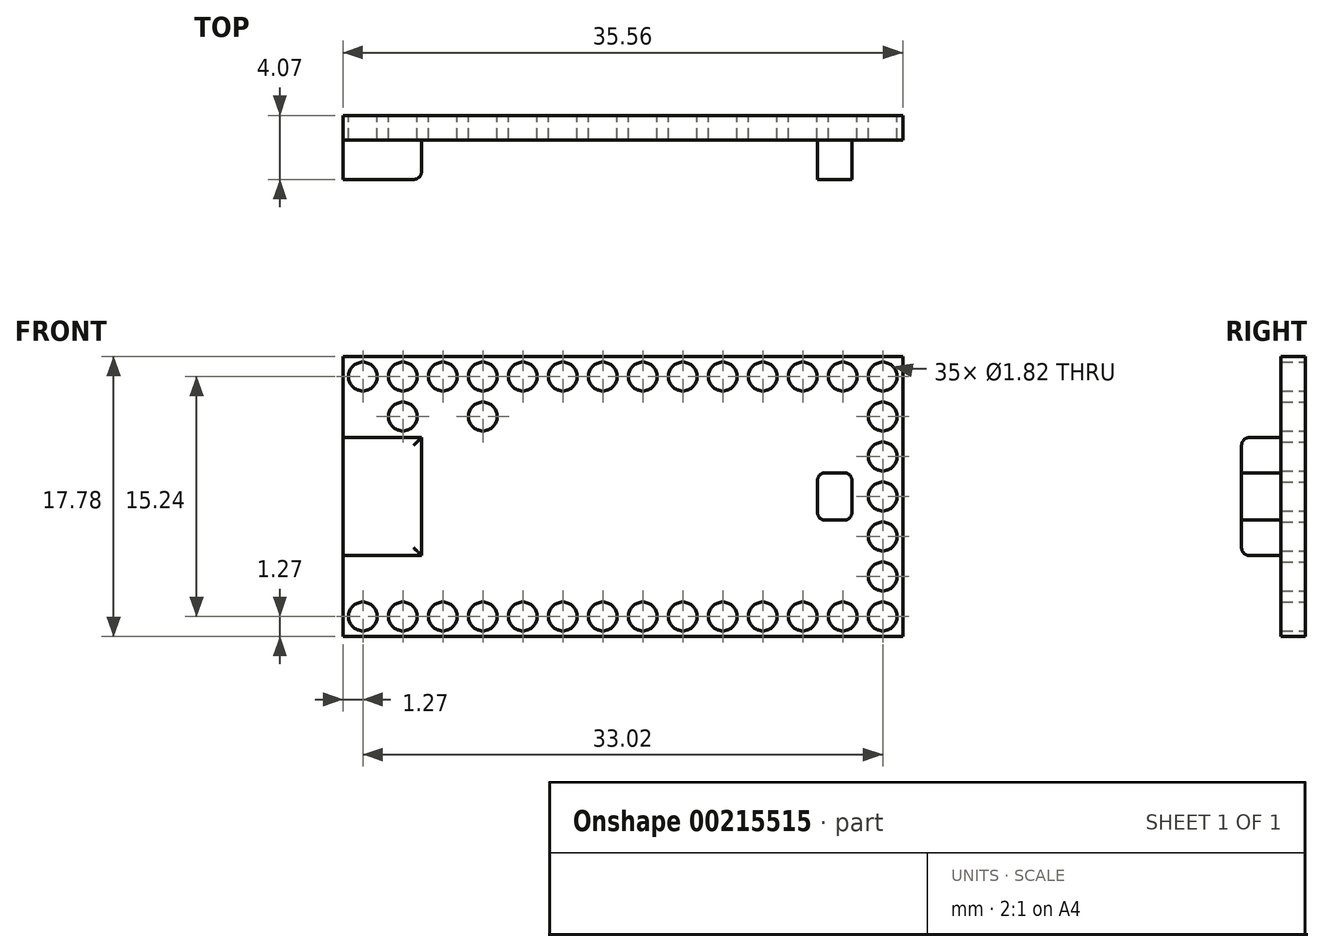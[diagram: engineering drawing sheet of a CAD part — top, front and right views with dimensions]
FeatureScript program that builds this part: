
annotation { "Feature Type Name" : "Feature", "Feature Type Description" : "" }
export const myFeature = defineFeature(function(context is Context, id is Id, definition is map)
    precondition{}
    {
        {
            var Q0;
            Q0=qCreatedBy(makeId("Front.planeOp"),FACE);
            var sketch = newSketch(context, id + "F0", { "sketchPlane" : qUnion([Q0])});
            skLineSegment(sketch, "E0.bottom", {"start": v(0, 0) * mm, "end": v(35.56, 0) * mm});
            skLineSegment(sketch, "E0.top", {"start": v(0, 17.78) * mm, "end": v(35.56, 17.78) * mm});
            skLineSegment(sketch, "E0.left", {"start": v(0, 0) * mm, "end": v(0, 17.78) * mm});
            skLineSegment(sketch, "E0.right", {"start": v(35.56, 0) * mm, "end": v(35.56, 17.78) * mm});
            skCircle(sketch, "E1", {"center": v(1.27, 16.51) * mm, "radius": 0.91 * mm});
            skCircle(sketch, "E2", {"center": v(3.8, 16.51) * mm, "radius": 0.91 * mm});
            skCircle(sketch, "E3.1.0.0", {"center": v(6.35, 16.51) * mm, "radius": 0.91 * mm});
            skCircle(sketch, "E3.2.0.0", {"center": v(8.89, 16.51) * mm, "radius": 0.91 * mm});
            skCircle(sketch, "E3.3.0.0", {"center": v(11.43, 16.51) * mm, "radius": 0.91 * mm});
            skCircle(sketch, "E3.4.0.0", {"center": v(13.97, 16.51) * mm, "radius": 0.91 * mm});
            skCircle(sketch, "E3.5.0.0", {"center": v(16.51, 16.51) * mm, "radius": 0.91 * mm});
            skCircle(sketch, "E3.6.0.0", {"center": v(19.05, 16.51) * mm, "radius": 0.91 * mm});
            skCircle(sketch, "E3.7.0.0", {"center": v(21.59, 16.51) * mm, "radius": 0.91 * mm});
            skCircle(sketch, "E3.8.0.0", {"center": v(24.13, 16.51) * mm, "radius": 0.91 * mm});
            skCircle(sketch, "E3.9.0.0", {"center": v(26.67, 16.51) * mm, "radius": 0.91 * mm});
            skCircle(sketch, "E3.10.0.0", {"center": v(29.21, 16.51) * mm, "radius": 0.91 * mm});
            skCircle(sketch, "E3.11.0.0", {"center": v(31.75, 16.51) * mm, "radius": 0.91 * mm});
            skCircle(sketch, "E3.12.0.0", {"center": v(34.3, 16.51) * mm, "radius": 0.91 * mm});
            skLineSegment(sketch, "E3.direction1", {"start": v(3.8, 16.51) * mm, "end": v(6.35, 16.51) * mm, "construction": true});
            skCircle(sketch, "E4", {"center": v(3.8, 13.97) * mm, "radius": 0.91 * mm});
            skLineSegment(sketch, "E5", {"start": v(0, 8.9) * mm, "end": v(35.56, 8.9) * mm, "construction": true});
            skLineSegment(sketch, "E6", {"start": v(34.3, 16.51) * mm, "end": v(34.3, 8.9) * mm, "construction": true});
            skCircle(sketch, "E7.1.0.0", {"center": v(34.3, 13.97) * mm, "radius": 0.91 * mm});
            skLineSegment(sketch, "E7.1.0.1", {"start": v(34.29, 13.97) * mm, "end": v(34.3, -2.54) * mm, "construction": true});
            skCircle(sketch, "E7.2.0.0", {"center": v(34.3, 11.43) * mm, "radius": 0.91 * mm});
            skLineSegment(sketch, "E7.2.0.1", {"start": v(34.3, 11.43) * mm, "end": v(34.3, -5.08) * mm, "construction": true});
            skLineSegment(sketch, "E7.direction1", {"start": v(34.29, 16.51) * mm, "end": v(34.29, 13.97) * mm, "construction": true});
            skArc(sketch, "E8.0.3.0", {"start": v(35.2, 8.9) * mm, "mid": v(34.3, 9.8) * mm, "end": v(33.38, 8.9) * mm});
            skLineSegment(sketch, "E8.2.3.0", {"start": v(34.3, 8.9) * mm, "end": v(34.3, -7.62) * mm, "construction": true});
            skLineSegment(sketch, "E9.trimOffspring", {"start": v(34.3, 7.98) * mm, "end": v(34.3, 0) * mm, "construction": true});
            skLineSegment(sketch, "E10.MirrorCS", {"start": v(34.3, 8.89) * mm, "end": v(34.3, 25.4) * mm, "construction": true});
            skLineSegment(sketch, "E11.MirrorCS", {"start": v(34.3, 6.35) * mm, "end": v(34.3, 22.86) * mm, "construction": true});
            skLineSegment(sketch, "E12.MirrorCS", {"start": v(34.29, 1.27) * mm, "end": v(34.29, 3.8) * mm, "construction": true});
            skLineSegment(sketch, "E13.MirrorCS", {"start": v(34.29, 3.8) * mm, "end": v(34.3, 20.32) * mm, "construction": true});
            skLineSegment(sketch, "E14.MirrorCS", {"start": v(3.8, 1.27) * mm, "end": v(6.35, 1.27) * mm, "construction": true});
            skCircle(sketch, "E15.MirrorC", {"center": v(1.27, 1.27) * mm, "radius": 0.91 * mm});
            skLineSegment(sketch, "E16.MirrorCS", {"start": v(35.56, 17.78) * mm, "end": v(35.56, 0) * mm});
            skLineSegment(sketch, "E17.MirrorCS", {"start": v(0, 17.78) * mm, "end": v(0, 0) * mm});
            skCircle(sketch, "E18.MirrorC", {"center": v(34.3, 6.35) * mm, "radius": 0.91 * mm});
            skCircle(sketch, "E19.MirrorC", {"center": v(21.59, 1.27) * mm, "radius": 0.91 * mm});
            skCircle(sketch, "E20.MirrorC", {"center": v(29.21, 1.27) * mm, "radius": 0.91 * mm});
            skCircle(sketch, "E21.MirrorC", {"center": v(11.43, 1.27) * mm, "radius": 0.91 * mm});
            skCircle(sketch, "E22.MirrorC", {"center": v(6.35, 1.27) * mm, "radius": 0.91 * mm});
            skCircle(sketch, "E23.MirrorC", {"center": v(19.05, 1.27) * mm, "radius": 0.91 * mm});
            skCircle(sketch, "E24.MirrorC", {"center": v(13.97, 1.27) * mm, "radius": 0.91 * mm});
            skCircle(sketch, "E25.MirrorC", {"center": v(26.67, 1.27) * mm, "radius": 0.91 * mm});
            skArc(sketch, "E26.MirrorCS", {"start": v(35.2, 8.9) * mm, "mid": v(34.3, 7.98) * mm, "end": v(33.38, 8.9) * mm});
            skCircle(sketch, "E27.MirrorC", {"center": v(3.8, 1.27) * mm, "radius": 0.91 * mm});
            skCircle(sketch, "E28.MirrorC", {"center": v(16.51, 1.27) * mm, "radius": 0.91 * mm});
            skCircle(sketch, "E29.MirrorC", {"center": v(34.3, 3.8) * mm, "radius": 0.91 * mm});
            skCircle(sketch, "E30.MirrorC", {"center": v(8.89, 1.27) * mm, "radius": 0.91 * mm});
            skLineSegment(sketch, "E31.MirrorCS", {"start": v(34.3, 1.27) * mm, "end": v(34.3, 8.89) * mm, "construction": true});
            skCircle(sketch, "E32.MirrorC", {"center": v(31.75, 1.27) * mm, "radius": 0.91 * mm});
            skCircle(sketch, "E33.MirrorC", {"center": v(34.3, 1.27) * mm, "radius": 0.91 * mm});
            skCircle(sketch, "E34.MirrorC", {"center": v(24.13, 1.27) * mm, "radius": 0.91 * mm});
            skCircle(sketch, "E35", {"center": v(8.89, 13.97) * mm, "radius": 0.91 * mm});
            skSolve(sketch);
        }
        {
            var Q0;
            Q0=makeQuery(id+"F0.imprint","IMPRINT",FACE,{"disambiguationData":[TD([[makeQuery(id+"F0.imprint","IMPRINT",EDGE,{"derivedFrom":sQuery(id+"F0.wireOp",EDGE,"E0.top")}),-1.0]])]});
            extrude(context, id + "F1", {"entities" : qUnion([Q0]), "depth" : 1.57 * mm});
        }
        {
            var Q0;
            Q0=makeQuery(id+"F1.opExtrude","CAP_FACE",FACE,{"disambiguationData":[OSD([sQuery(id+"F0.wireOp",EDGE,"E0.top"),sQuery(id+"F0.wireOp",EDGE,"E1"),sQuery(id+"F0.wireOp",EDGE,"E2"),sQuery(id+"F0.wireOp",EDGE,"E3.1.0.0"),sQuery(id+"F0.wireOp",EDGE,"E3.2.0.0"),sQuery(id+"F0.wireOp",EDGE,"E3.3.0.0"),sQuery(id+"F0.wireOp",EDGE,"E3.4.0.0"),sQuery(id+"F0.wireOp",EDGE,"E3.5.0.0"),sQuery(id+"F0.wireOp",EDGE,"E3.6.0.0"),sQuery(id+"F0.wireOp",EDGE,"E3.7.0.0"),sQuery(id+"F0.wireOp",EDGE,"E3.8.0.0"),sQuery(id+"F0.wireOp",EDGE,"E3.9.0.0"),sQuery(id+"F0.wireOp",EDGE,"E3.10.0.0"),sQuery(id+"F0.wireOp",EDGE,"E3.11.0.0"),sQuery(id+"F0.wireOp",EDGE,"E3.12.0.0"),sQuery(id+"F0.wireOp",EDGE,"E4"),sQuery(id+"F0.wireOp",EDGE,"E7.1.0.0"),sQuery(id+"F0.wireOp",EDGE,"E7.2.0.0"),sQuery(id+"F0.wireOp",EDGE,"E8.0.3.0"),sQuery(id+"F0.wireOp",EDGE,"E15.MirrorC"),sQuery(id+"F0.wireOp",EDGE,"E16.MirrorCS"),sQuery(id+"F0.wireOp",EDGE,"E17.MirrorCS"),sQuery(id+"F0.wireOp",EDGE,"E18.MirrorC"),sQuery(id+"F0.wireOp",EDGE,"E19.MirrorC"),sQuery(id+"F0.wireOp",EDGE,"E0.bottom"),sQuery(id+"F0.wireOp",EDGE,"E20.MirrorC"),sQuery(id+"F0.wireOp",EDGE,"E21.MirrorC"),sQuery(id+"F0.wireOp",EDGE,"E22.MirrorC"),sQuery(id+"F0.wireOp",EDGE,"E23.MirrorC"),sQuery(id+"F0.wireOp",EDGE,"E24.MirrorC"),sQuery(id+"F0.wireOp",EDGE,"E25.MirrorC"),sQuery(id+"F0.wireOp",EDGE,"E26.MirrorCS"),sQuery(id+"F0.wireOp",EDGE,"E27.MirrorC"),sQuery(id+"F0.wireOp",EDGE,"E28.MirrorC"),sQuery(id+"F0.wireOp",EDGE,"E29.MirrorC"),sQuery(id+"F0.wireOp",EDGE,"E30.MirrorC"),sQuery(id+"F0.wireOp",EDGE,"E32.MirrorC"),sQuery(id+"F0.wireOp",EDGE,"E33.MirrorC"),sQuery(id+"F0.wireOp",EDGE,"E34.MirrorC"),sQuery(id+"F0.wireOp",EDGE,"E35")])],"isStart":false});
            var sketch = newSketch(context, id + "F2", { "sketchPlane" : qUnion([Q0])});
            skLineSegment(sketch, "E36", {"start": v(5, 8.9) * mm, "end": v(35.56, 8.9) * mm, "construction": true});
            skLineSegment(sketch, "E37.top", {"start": v(0, 12.64) * mm, "end": v(5, 12.64) * mm});
            skLineSegment(sketch, "E37.left", {"start": v(0, 8.9) * mm, "end": v(0, 12.64) * mm});
            skLineSegment(sketch, "E37.right", {"start": v(5, 8.9) * mm, "end": v(5, 12.64) * mm});
            skLineSegment(sketch, "E38", {"start": v(5, 8.9) * mm, "end": v(0, 8.9) * mm, "construction": true});
            skLineSegment(sketch, "E39.MirrorCS", {"start": v(5, 8.9) * mm, "end": v(5, 5.14) * mm});
            skLineSegment(sketch, "E40.MirrorCS", {"start": v(0, 5.14) * mm, "end": v(5, 5.14) * mm});
            skLineSegment(sketch, "E41.MirrorCS", {"start": v(0, 8.9) * mm, "end": v(0, 5.14) * mm});
            skSolve(sketch);
        }
        {
            var Q0;
            Q0=makeQuery(id+"F2.imprint","IMPRINT",FACE,{"disambiguationData":[TD([[makeQuery(id+"F2.imprint","IMPRINT",EDGE,{"derivedFrom":sQuery(id+"F2.wireOp",EDGE,"E37.top")}),-1.0]])]});
            extrude(context, id + "F3", {"entities" : qUnion([Q0]), "operationType" : NewBodyOperationType.ADD, "depth" : 2.5 * mm});
        }
        {
            var Q0;
            Q0=makeQuery(id+"F3.opExtrude","CAP_EDGE",EDGE,{"disambiguationData":[OSD([sQuery(id+"F2.wireOp",EDGE,"E40.MirrorCS")])],"isStart":false});
            var Q1;
            Q1=makeQuery(id+"F3.opExtrude","CAP_EDGE",EDGE,{"disambiguationData":[OSD([sQuery(id+"F2.wireOp",EDGE,"E37.top")])],"isStart":false});
            var Q2;
            Q2=makeQuery(id+"F3.opExtrude","CAP_EDGE",EDGE,{"disambiguationData":[OSD([sQuery(id+"F2.wireOp",EDGE,"E37.right"),sQuery(id+"F2.wireOp",EDGE,"E39.MirrorCS")])],"isStart":false});
            fillet(context, id + "F4", {"entities" : qUnion([Q0, Q1, Q2]), "radius" : 0.5 * mm, "tangentPropagation" : true, "allowEdgeOverflow" : false});
        }
        {
            var Q0;
            Q0=makeQuery(id+"F1.opExtrude","CAP_FACE",FACE,{"disambiguationData":[OSD([sQuery(id+"F0.wireOp",EDGE,"E0.top"),sQuery(id+"F0.wireOp",EDGE,"E1"),sQuery(id+"F0.wireOp",EDGE,"E2"),sQuery(id+"F0.wireOp",EDGE,"E3.1.0.0"),sQuery(id+"F0.wireOp",EDGE,"E3.2.0.0"),sQuery(id+"F0.wireOp",EDGE,"E3.3.0.0"),sQuery(id+"F0.wireOp",EDGE,"E3.4.0.0"),sQuery(id+"F0.wireOp",EDGE,"E3.5.0.0"),sQuery(id+"F0.wireOp",EDGE,"E3.6.0.0"),sQuery(id+"F0.wireOp",EDGE,"E3.7.0.0"),sQuery(id+"F0.wireOp",EDGE,"E3.8.0.0"),sQuery(id+"F0.wireOp",EDGE,"E3.9.0.0"),sQuery(id+"F0.wireOp",EDGE,"E3.10.0.0"),sQuery(id+"F0.wireOp",EDGE,"E3.11.0.0"),sQuery(id+"F0.wireOp",EDGE,"E3.12.0.0"),sQuery(id+"F0.wireOp",EDGE,"E4"),sQuery(id+"F0.wireOp",EDGE,"E7.1.0.0"),sQuery(id+"F0.wireOp",EDGE,"E7.2.0.0"),sQuery(id+"F0.wireOp",EDGE,"E8.0.3.0"),sQuery(id+"F0.wireOp",EDGE,"E15.MirrorC"),sQuery(id+"F0.wireOp",EDGE,"E16.MirrorCS"),sQuery(id+"F0.wireOp",EDGE,"E17.MirrorCS"),sQuery(id+"F0.wireOp",EDGE,"E18.MirrorC"),sQuery(id+"F0.wireOp",EDGE,"E19.MirrorC"),sQuery(id+"F0.wireOp",EDGE,"E0.bottom"),sQuery(id+"F0.wireOp",EDGE,"E20.MirrorC"),sQuery(id+"F0.wireOp",EDGE,"E21.MirrorC"),sQuery(id+"F0.wireOp",EDGE,"E22.MirrorC"),sQuery(id+"F0.wireOp",EDGE,"E23.MirrorC"),sQuery(id+"F0.wireOp",EDGE,"E24.MirrorC"),sQuery(id+"F0.wireOp",EDGE,"E25.MirrorC"),sQuery(id+"F0.wireOp",EDGE,"E26.MirrorCS"),sQuery(id+"F0.wireOp",EDGE,"E27.MirrorC"),sQuery(id+"F0.wireOp",EDGE,"E28.MirrorC"),sQuery(id+"F0.wireOp",EDGE,"E29.MirrorC"),sQuery(id+"F0.wireOp",EDGE,"E30.MirrorC"),sQuery(id+"F0.wireOp",EDGE,"E32.MirrorC"),sQuery(id+"F0.wireOp",EDGE,"E33.MirrorC"),sQuery(id+"F0.wireOp",EDGE,"E34.MirrorC"),sQuery(id+"F0.wireOp",EDGE,"E35")])],"isStart":false});
            var sketch = newSketch(context, id + "F5", { "sketchPlane" : qUnion([Q0])});
            skLineSegment(sketch, "E42", {"start": v(35.56, 8.9) * mm, "end": v(21.42, 8.9) * mm, "construction": true});
            skLineSegment(sketch, "E43", {"start": v(1.27, 16.51) * mm, "end": v(1.27, 20.15) * mm, "construction": true});
            skLineSegment(sketch, "E44.bottom", {"start": v(30.14, 8.9) * mm, "end": v(31.24, 8.9) * mm});
            skLineSegment(sketch, "E44.top", {"start": v(30.14, 10.4) * mm, "end": v(31.24, 10.4) * mm});
            skLineSegment(sketch, "E44.left", {"start": v(30.14, 8.9) * mm, "end": v(30.14, 10.4) * mm});
            skLineSegment(sketch, "E45.bottom", {"start": v(31.24, 10.4) * mm, "end": v(32.34, 10.4) * mm});
            skLineSegment(sketch, "E45.top", {"start": v(31.24, 8.9) * mm, "end": v(32.34, 8.9) * mm});
            skLineSegment(sketch, "E45.right", {"start": v(32.34, 10.4) * mm, "end": v(32.34, 8.9) * mm});
            skLineSegment(sketch, "E46.MirrorCS", {"start": v(30.14, 8.9) * mm, "end": v(30.14, 7.4) * mm});
            skLineSegment(sketch, "E47.MirrorCS", {"start": v(30.14, 7.4) * mm, "end": v(31.24, 7.4) * mm});
            skLineSegment(sketch, "E48.MirrorCS", {"start": v(31.24, 7.4) * mm, "end": v(32.34, 7.4) * mm});
            skLineSegment(sketch, "E49.MirrorCS", {"start": v(32.34, 7.4) * mm, "end": v(32.34, 8.9) * mm});
            skSolve(sketch);
        }
        {
            var Q0;
            Q0=makeQuery(id+"F5.imprint","IMPRINT",FACE,{"disambiguationData":[TD([[makeQuery(id+"F5.imprint","IMPRINT",EDGE,{"derivedFrom":sQuery(id+"F5.wireOp",EDGE,"E44.bottom")}),-1.0]])]});
            var Q1;
            Q1=makeQuery(id+"F5.imprint","IMPRINT",FACE,{"disambiguationData":[TD([[makeQuery(id+"F5.imprint","IMPRINT",EDGE,{"derivedFrom":sQuery(id+"F5.wireOp",EDGE,"E44.bottom")}),1.0]])]});
            extrude(context, id + "F6", {"entities" : qUnion([Q0, Q1]), "operationType" : NewBodyOperationType.ADD, "depth" : 2.5 * mm});
        }
        {
            var Q0;
            Q0=makeQuery(id+"F6.opExtrude","SWEPT_EDGE",EDGE,{"disambiguationData":[OSD([sQuery(id+"F5.wireOp",EDGE,"E46.MirrorCS"),sQuery(id+"F5.wireOp",EDGE,"E47.MirrorCS")])]});
            var Q1;
            Q1=makeQuery(id+"F6.opExtrude","SWEPT_EDGE",EDGE,{"disambiguationData":[OSD([sQuery(id+"F5.wireOp",EDGE,"E48.MirrorCS"),sQuery(id+"F5.wireOp",EDGE,"E49.MirrorCS")])]});
            var Q2;
            Q2=makeQuery(id+"F6.opExtrude","SWEPT_EDGE",EDGE,{"disambiguationData":[OSD([sQuery(id+"F5.wireOp",EDGE,"E44.top"),sQuery(id+"F5.wireOp",EDGE,"E44.left")])]});
            var Q3;
            Q3=makeQuery(id+"F6.opExtrude","SWEPT_EDGE",EDGE,{"disambiguationData":[OSD([sQuery(id+"F5.wireOp",EDGE,"E45.bottom"),sQuery(id+"F5.wireOp",EDGE,"E45.right")])]});
            fillet(context, id + "F7", {"entities" : qUnion([Q0, Q1, Q2, Q3]), "radius" : 0.5 * mm, "tangentPropagation" : true, "allowEdgeOverflow" : false});
        }
    });
